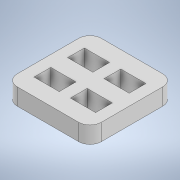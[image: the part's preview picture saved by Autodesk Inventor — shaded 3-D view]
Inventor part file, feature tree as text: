
AUTODESK INVENTOR PART (.ipt)
format: ipt  version: 2020 (Build 240168000, 168)  size: 125,952 bytes
history: native  units: in
note: dims shown in document units (in); Inventor stores cm internally (conversion verified against a paired STEP export)
features: extrude x1, sketch x1
ambient origin geometry x8: Origin, YZ Plane, XZ Plane, XY Plane, X Axis, Y Axis, Z Axis, Center Point
bodies: Solid1 (feature_tree)
feature tree (2):
  extrude  "Extrusion1"  Depth=0.4331in
  sketch  "Sketch1"  dims[d0=0.0787in d1=0.4331in d2=0.4331in d5=0.1181in d6=0.1772in d7=0.0787in d8=0.1181in d11=0.1181in d12=0.0in]
